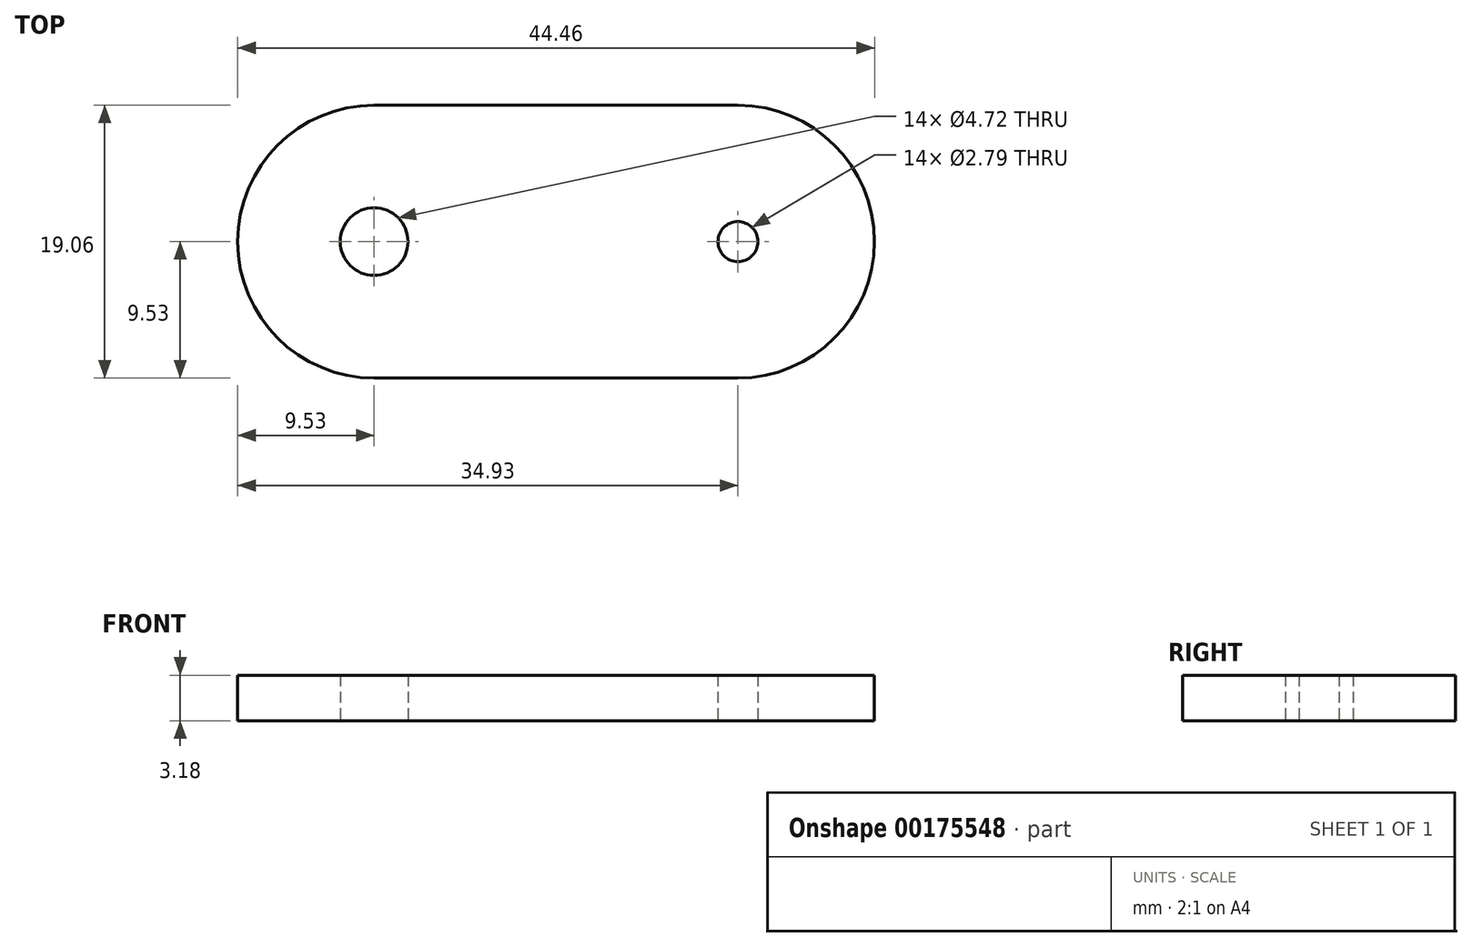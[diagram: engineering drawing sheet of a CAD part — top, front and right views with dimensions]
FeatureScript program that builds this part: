
annotation { "Feature Type Name" : "Feature", "Feature Type Description" : "" }
export const myFeature = defineFeature(function(context is Context, id is Id, definition is map)
    precondition{}
    {
        {
            var Q0;
            Q0=qCreatedBy(makeId("Top.planeOp"),FACE);
            var sketch = newSketch(context, id + "F0", { "sketchPlane" : qUnion([Q0])});
            skLineSegment(sketch, "E0.bottom", {"start": v(12.7, 9.53) * mm, "end": v(-12.7, 9.53) * mm});
            skLineSegment(sketch, "E0.top", {"start": v(12.7, -9.53) * mm, "end": v(-12.7, -9.53) * mm});
            skPoint(sketch, "E0.middle", {"position": v(0, 0) * mm});
            skArc(sketch, "E1", {"start": v(-12.7, 9.53) * mm, "mid": v(-22.23, 0) * mm, "end": v(-12.7, -9.53) * mm});
            skArc(sketch, "E2", {"start": v(12.7, -9.53) * mm, "mid": v(22.23, 0) * mm, "end": v(12.7, 9.53) * mm});
            skCircle(sketch, "E3", {"center": v(-12.7, 0) * mm, "radius": 2.36 * mm});
            skCircle(sketch, "E4", {"center": v(12.7, 0) * mm, "radius": 1.4 * mm});
            skSolve(sketch);
        }
        {
            var Q0;
            Q0 = qSketchRegion(id + "F0", true);
            extrude(context, id + "F1", {"entities" : qUnion([Q0]), "depth" : 3.17 * mm});
        }
    });
